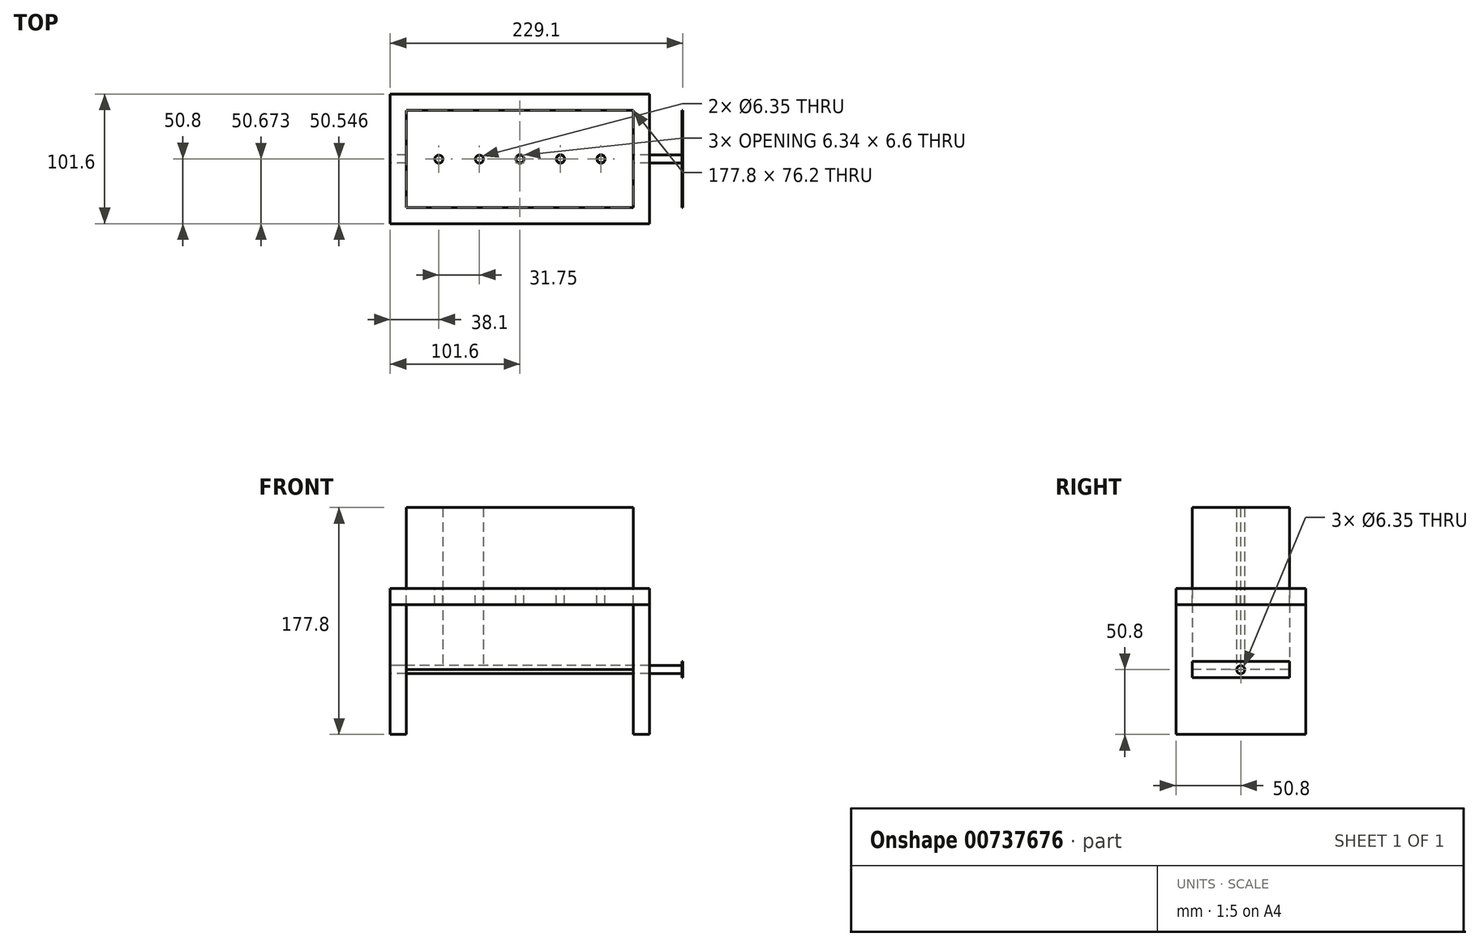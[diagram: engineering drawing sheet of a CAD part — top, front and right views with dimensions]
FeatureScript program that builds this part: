
annotation { "Feature Type Name" : "Feature", "Feature Type Description" : "" }
export const myFeature = defineFeature(function(context is Context, id is Id, definition is map)
    precondition{}
    {
        {
            assignVariable(context, id + "F0", {"name" : "w", "anyValue" : .5});
        }
        {
            var Q0;
            Q0=qCreatedBy(makeId("Front.planeOp"),FACE);
            var sketch = newSketch(context, id + "F1", { "sketchPlane" : qUnion([Q0])});
            skLineSegment(sketch, "E0.bottom", {"start": v(-101.6, 63.5) * mm, "end": v(101.6, 63.5) * mm});
            skLineSegment(sketch, "E0.top", {"start": v(-101.6, -63.5) * mm, "end": v(101.6, -63.5) * mm});
            skLineSegment(sketch, "E0.left", {"start": v(-101.6, 63.5) * mm, "end": v(-101.6, -63.5) * mm});
            skLineSegment(sketch, "E0.right", {"start": v(101.6, 63.5) * mm, "end": v(101.6, -63.5) * mm});
            skPoint(sketch, "E0.middle", {"position": v(0, 0) * mm});
            skLineSegment(sketch, "E1.bottom", {"start": v(-88.9, 50.8) * mm, "end": v(88.9, 50.8) * mm});
            skLineSegment(sketch, "E1.top", {"start": v(-88.9, -50.8) * mm, "end": v(88.9, -50.8) * mm});
            skLineSegment(sketch, "E1.left", {"start": v(-88.9, 50.8) * mm, "end": v(-88.9, -50.8) * mm});
            skLineSegment(sketch, "E1.right", {"start": v(88.9, 50.8) * mm, "end": v(88.9, -50.8) * mm});
            skLineSegment(sketch, "E2.top", {"start": v(-101.6, 50.8) * mm, "end": v(101.6, 50.8) * mm});
            skLineSegment(sketch, "E2.left", {"start": v(-101.6, 63.5) * mm, "end": v(-101.6, 50.8) * mm});
            skLineSegment(sketch, "E2.right", {"start": v(101.6, 63.5) * mm, "end": v(101.6, 50.8) * mm});
            skLineSegment(sketch, "E3.left", {"start": v(-101.6, -63.5) * mm, "end": v(-101.6, -63.5) * mm});
            skLineSegment(sketch, "E4.bottom", {"start": v(101.6, -63.5) * mm, "end": v(-101.6, -63.5) * mm});
            skLineSegment(sketch, "E4.top", {"start": v(101.6, -50.8) * mm, "end": v(-101.6, -50.8) * mm});
            skLineSegment(sketch, "E4.left", {"start": v(101.6, -63.5) * mm, "end": v(101.6, -50.8) * mm});
            skLineSegment(sketch, "E4.right", {"start": v(-101.6, -63.5) * mm, "end": v(-101.6, -50.8) * mm});
            skSolve(sketch);
        }
        {
            var Q0;
            Q0=makeQuery(id+"F1.imprint","IMPRINT",FACE,{"disambiguationData":[TD([[makeQuery(id+"F1.imprint","IMPRINT",EDGE,{"derivedFrom":sQuery(id+"F1.wireOp",EDGE,"E4.bottom")}),-1.0]])]});
            var Q1;
            Q1=makeQuery(id+"F1.imprint","IMPRINT",FACE,{"disambiguationData":[TD([[makeQuery(id+"F1.imprint","IMPRINT",EDGE,{"derivedFrom":sQuery(id+"F1.wireOp",EDGE,"E0.bottom")}),-1.0]])]});
            extrude(context, id + "F2", {"entities" : qUnion([Q0, Q1]), "endBound" : BoundingType.SYMMETRIC, "depth" : 101.6 * mm, "offsetDistance" : 25.4 * mm});
        }
        {
            var Q0;
            {var subQ0=sQuery(id+"F1.wireOp",EDGE,"E0.left");Q0=makeQuery(id+"F1.imprint","IMPRINT",FACE,{"disambiguationData":[TD([[makeQuery(id+"F1.imprint","IMPRINT",EDGE,{"derivedFrom":subQ0}),1.0]])]});}
            var Q1;
            {var subQ0=sQuery(id+"F1.wireOp",EDGE,"E0.right");Q1=makeQuery(id+"F1.imprint","IMPRINT",FACE,{"disambiguationData":[TD([[makeQuery(id+"F1.imprint","IMPRINT",EDGE,{"derivedFrom":subQ0}),-1.0]])]});}
            extrude(context, id + "F3", {"entities" : qUnion([Q0, Q1]), "endBound" : BoundingType.SYMMETRIC, "depth" : 101.6 * mm, "offsetDistance" : 25.4 * mm});
        }
        {
            var Q0;
            Q0=makeQuery(id+"F3.opExtrude","SWEPT_FACE",FACE,{"disambiguationData":[OSD([sQuery(id+"F1.wireOp",EDGE,"E0.left")])]});
            var sketch = newSketch(context, id + "F4", { "sketchPlane" : qUnion([Q0])});
            skCircle(sketch, "E5", {"center": v(0, 0) * mm, "radius": 3.18 * mm});
            skSolve(sketch);
        }
        {
            var Q0;
            Q0=makeQuery(id+"F4.imprint","IMPRINT",FACE,{"disambiguationData":[TD([[makeQuery(id+"F4.imprint","IMPRINT",EDGE,{"derivedFrom":sQuery(id+"F4.wireOp",EDGE,"E5")}),1.0]])]});
            extrude(context, id + "F5", {"entities" : qUnion([Q0]), "operationType" : NewBodyOperationType.REMOVE, "endBound" : BoundingType.THROUGH_ALL, "oppositeDirection" : true, "depth" : 25.4 * mm, "offsetDistance" : 25.4 * mm});
        }
        {
            var Q0;
            Q0=makeQuery(id+"F4.imprint","IMPRINT",FACE,{"disambiguationData":[TD([[makeQuery(id+"F4.imprint","IMPRINT",EDGE,{"derivedFrom":sQuery(id+"F4.wireOp",EDGE,"E5")}),1.0]])]});
            extrude(context, id + "F6", {"entities" : qUnion([Q0]), "oppositeDirection" : true, "depth" : 228.6 * mm, "offsetDistance" : 25.4 * mm});
        }
        {
            var Q0;
            Q0=makeQuery(id+"F6.opExtrude","CAP_FACE",FACE,{"disambiguationData":[OSD([sQuery(id+"F4.wireOp",EDGE,"E5")])],"isStart":false});
            var sketch = newSketch(context, id + "F7", { "sketchPlane" : qUnion([Q0])});
            skLineSegment(sketch, "E6.bottom", {"start": v(38.1, 6.35) * mm, "end": v(-38.1, 6.35) * mm});
            skLineSegment(sketch, "E6.top", {"start": v(38.1, -6.35) * mm, "end": v(-38.1, -6.35) * mm});
            skLineSegment(sketch, "E6.left", {"start": v(38.1, 6.35) * mm, "end": v(38.1, -6.35) * mm});
            skLineSegment(sketch, "E6.right", {"start": v(-38.1, 6.35) * mm, "end": v(-38.1, -6.35) * mm});
            skPoint(sketch, "E6.middle", {"position": v(0, 0) * mm});
            skSolve(sketch);
        }
        {
            var Q0;
            Q0=makeQuery(id+"F7.imprint","IMPRINT",FACE,{"disambiguationData":[TD([[makeQuery(id+"F7.imprint","IMPRINT",EDGE,{"derivedFrom":sQuery(id+"F7.wireOp",EDGE,"E6.bottom")}),1.0]])]});
            extrude(context, id + "F8", {"entities" : qUnion([Q0]), "depth" : (getVariable(context, 'w')) * mm, "offsetDistance" : 25.4 * mm});
        }
        {
            var Q0;
            Q0=makeQuery(id+"F2.opExtrude","SWEPT_FACE",FACE,{"disambiguationData":[OSD([sQuery(id+"F1.wireOp",EDGE,"E0.bottom")])]});
            var sketch = newSketch(context, id + "F9", { "sketchPlane" : qUnion([Q0])});
            skLineSegment(sketch, "E7.bottom", {"start": v(88.9, 38.1) * mm, "end": v(-88.9, 38.1) * mm});
            skLineSegment(sketch, "E7.top", {"start": v(88.9, -38.1) * mm, "end": v(-88.9, -38.1) * mm});
            skLineSegment(sketch, "E7.left", {"start": v(88.9, 38.1) * mm, "end": v(88.9, -38.1) * mm});
            skLineSegment(sketch, "E7.right", {"start": v(-88.9, 38.1) * mm, "end": v(-88.9, -38.1) * mm});
            skPoint(sketch, "E7.middle", {"position": v(0, 0) * mm});
            skCircle(sketch, "E8", {"center": v(0, 0) * mm, "radius": 3.18 * mm});
            skCircle(sketch, "E9.0.1.0", {"center": v(0, -0.25) * mm, "radius": 3.18 * mm});
            skCircle(sketch, "E9.1.0.0", {"center": v(31.75, 0) * mm, "radius": 3.18 * mm});
            skCircle(sketch, "E9.1.1.0", {"center": v(31.75, -0.25) * mm, "radius": 3.18 * mm});
            skCircle(sketch, "E9.2.0.0", {"center": v(63.5, 0) * mm, "radius": 3.18 * mm});
            skCircle(sketch, "E9.2.1.0", {"center": v(63.5, -0.25) * mm, "radius": 3.18 * mm});
            skLineSegment(sketch, "E9.direction1", {"start": v(0, 0) * mm, "end": v(31.75, 0) * mm, "construction": true});
            skLineSegment(sketch, "E9.direction2", {"start": v(0, 0) * mm, "end": v(0, -0.25) * mm, "construction": true});
            skCircle(sketch, "E10.MirrorC", {"center": v(-31.75, -0.25) * mm, "radius": 3.18 * mm});
            skCircle(sketch, "E11.MirrorC", {"center": v(-63.5, -0.25) * mm, "radius": 3.18 * mm});
            skSolve(sketch);
        }
        {
            var Q0;
            Q0=makeQuery(id+"F9.imprint","IMPRINT",FACE,{"disambiguationData":[TD([[makeQuery(id+"F9.imprint","IMPRINT",EDGE,{"derivedFrom":sQuery(id+"F9.wireOp",EDGE,"E11.MirrorC")}),-1.0]])]});
            var Q1;
            Q1=makeQuery(id+"F9.imprint","IMPRINT",FACE,{"disambiguationData":[TD([[makeQuery(id+"F9.imprint","IMPRINT",EDGE,{"derivedFrom":sQuery(id+"F9.wireOp",EDGE,"E10.MirrorC")}),-1.0]])]});
            var Q2;
            {var subQ0=sQuery(id+"F9.wireOp",EDGE,"E9.0.1.0");var subQ1=sQuery(id+"F9.wireOp",EDGE,"E8");var subQ2=makeQuery(id+"F9.imprint","INTERSECT",VERTEX,{"disambiguationData":[OD(0.0)],"derivedFrom":[subQ1,subQ0]});Q2=makeQuery(id+"F9.imprint","IMPRINT",FACE,{"disambiguationData":[TD([[makeQuery(id+"F9.imprint","IMPRINT",EDGE,{"disambiguationData":[TD([[subQ2,-1.0]])],"derivedFrom":subQ1}),1.0]])]});}
            var Q3;
            {var subQ0=sQuery(id+"F9.wireOp",EDGE,"E9.1.1.0");var subQ1=sQuery(id+"F9.wireOp",EDGE,"E9.1.0.0");var subQ2=makeQuery(id+"F9.imprint","INTERSECT",VERTEX,{"disambiguationData":[OD(0.0)],"derivedFrom":[subQ1,subQ0]});Q3=makeQuery(id+"F9.imprint","IMPRINT",FACE,{"disambiguationData":[TD([[makeQuery(id+"F9.imprint","IMPRINT",EDGE,{"disambiguationData":[TD([[subQ2,-1.0]])],"derivedFrom":subQ1}),1.0]])]});}
            var Q4;
            {var subQ0=sQuery(id+"F9.wireOp",EDGE,"E9.2.1.0");var subQ1=sQuery(id+"F9.wireOp",EDGE,"E9.2.0.0");var subQ2=makeQuery(id+"F9.imprint","INTERSECT",VERTEX,{"disambiguationData":[OD(0.0)],"derivedFrom":[subQ1,subQ0]});Q4=makeQuery(id+"F9.imprint","IMPRINT",FACE,{"disambiguationData":[TD([[makeQuery(id+"F9.imprint","IMPRINT",EDGE,{"disambiguationData":[TD([[subQ2,-1.0]])],"derivedFrom":subQ1}),1.0]])]});}
            extrude(context, id + "F10", {"entities" : qUnion([Q0, Q1, Q2, Q3, Q4]), "operationType" : NewBodyOperationType.REMOVE, "endBound" : BoundingType.UP_TO_NEXT, "oppositeDirection" : true, "depth" : 25.4 * mm, "offsetDistance" : 25.4 * mm});
        }
        {
            var Q0;
            Q0=makeQuery(id+"F9.imprint","IMPRINT",FACE,{"disambiguationData":[TD([[makeQuery(id+"F9.imprint","IMPRINT",EDGE,{"derivedFrom":sQuery(id+"F9.wireOp",EDGE,"E11.MirrorC")}),-1.0]])]});
            var Q1;
            Q1=makeQuery(id+"F9.imprint","IMPRINT",FACE,{"disambiguationData":[TD([[makeQuery(id+"F9.imprint","IMPRINT",EDGE,{"derivedFrom":sQuery(id+"F9.wireOp",EDGE,"E10.MirrorC")}),-1.0]])]});
            var Q2;
            {var subQ0=sQuery(id+"F9.wireOp",EDGE,"E9.0.1.0");var subQ1=sQuery(id+"F9.wireOp",EDGE,"E8");var subQ2=makeQuery(id+"F9.imprint","INTERSECT",VERTEX,{"disambiguationData":[OD(0.0)],"derivedFrom":[subQ1,subQ0]});Q2=makeQuery(id+"F9.imprint","IMPRINT",FACE,{"disambiguationData":[TD([[makeQuery(id+"F9.imprint","IMPRINT",EDGE,{"disambiguationData":[TD([[subQ2,-1.0]])],"derivedFrom":subQ1}),1.0]])]});}
            var Q3;
            {var subQ0=sQuery(id+"F9.wireOp",EDGE,"E9.1.1.0");var subQ1=sQuery(id+"F9.wireOp",EDGE,"E9.1.0.0");var subQ2=makeQuery(id+"F9.imprint","INTERSECT",VERTEX,{"disambiguationData":[OD(0.0)],"derivedFrom":[subQ1,subQ0]});Q3=makeQuery(id+"F9.imprint","IMPRINT",FACE,{"disambiguationData":[TD([[makeQuery(id+"F9.imprint","IMPRINT",EDGE,{"disambiguationData":[TD([[subQ2,-1.0]])],"derivedFrom":subQ1}),1.0]])]});}
            var Q4;
            {var subQ0=sQuery(id+"F9.wireOp",EDGE,"E9.2.1.0");var subQ1=sQuery(id+"F9.wireOp",EDGE,"E9.2.0.0");var subQ2=makeQuery(id+"F9.imprint","INTERSECT",VERTEX,{"disambiguationData":[OD(0.0)],"derivedFrom":[subQ1,subQ0]});Q4=makeQuery(id+"F9.imprint","IMPRINT",FACE,{"disambiguationData":[TD([[makeQuery(id+"F9.imprint","IMPRINT",EDGE,{"disambiguationData":[TD([[subQ2,-1.0]])],"derivedFrom":subQ1}),1.0]])]});}
            extrude(context, id + "F11", {"entities" : qUnion([Q0, Q1, Q2, Q3, Q4]), "endBound" : BoundingType.SYMMETRIC, "depth" : 127 * mm, "offsetDistance" : 25.4 * mm});
        }
    });
